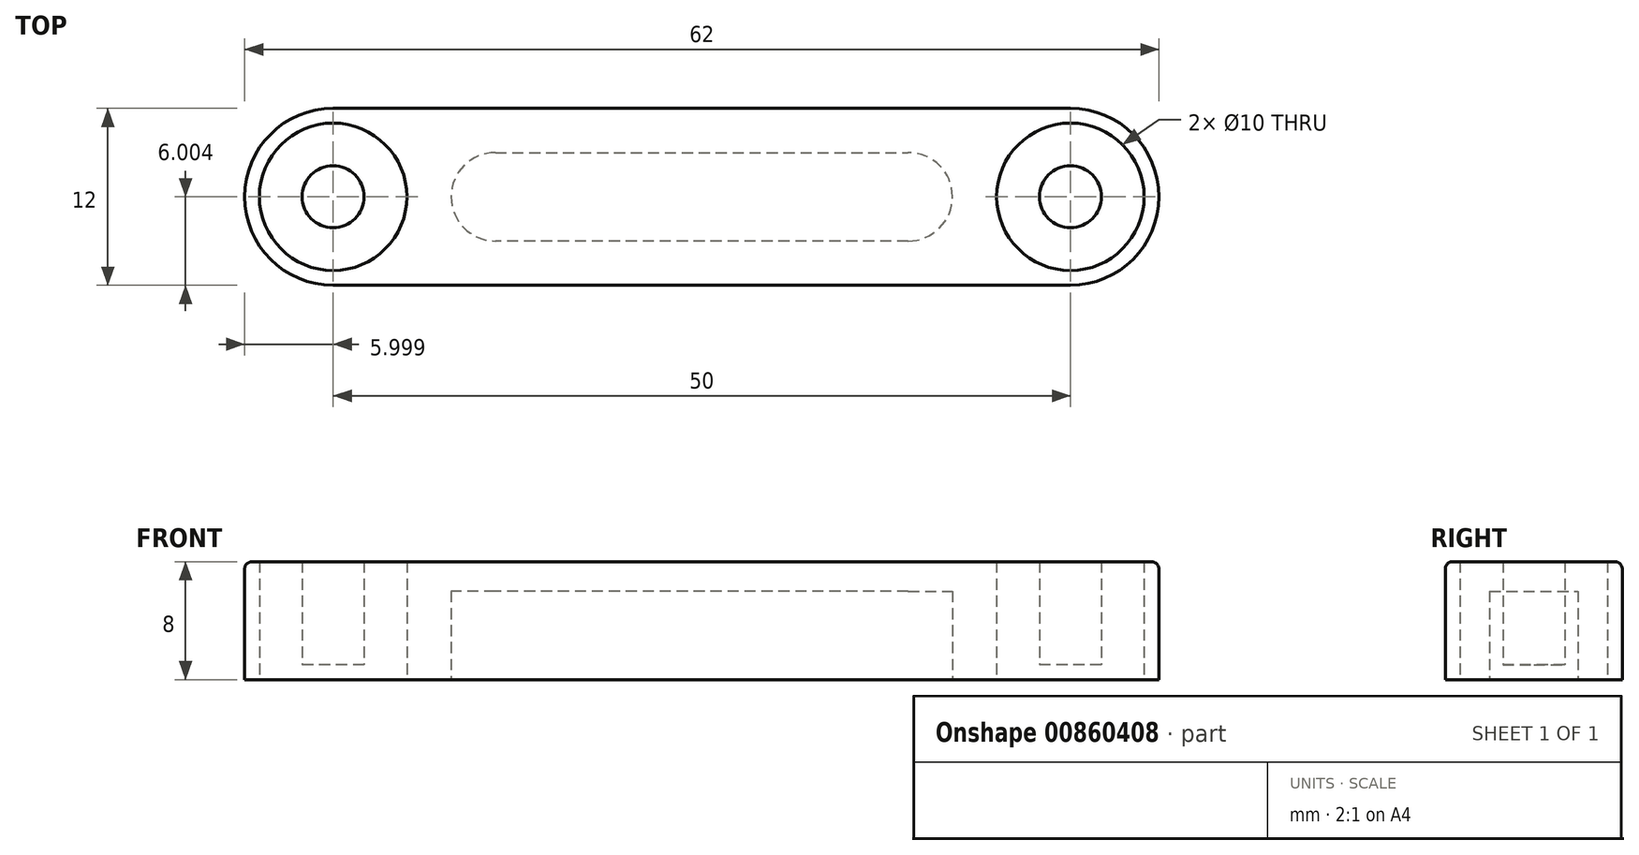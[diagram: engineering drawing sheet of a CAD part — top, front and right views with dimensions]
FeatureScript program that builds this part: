
annotation { "Feature Type Name" : "Feature", "Feature Type Description" : "" }
export const myFeature = defineFeature(function(context is Context, id is Id, definition is map)
    precondition{}
    {
        {
            var Q0;
            Q0=qCreatedBy(makeId("Top.planeOp"),FACE);
            var sketch = newSketch(context, id + "F0", { "sketchPlane" : qUnion([Q0])});
            skLineSegment(sketch, "E0", {"start": v(-96.16, -25.4) * mm, "end": v(-46.16, -25.4) * mm});
            skLineSegment(sketch, "E1", {"start": v(-46.16, -13.4) * mm, "end": v(-96.16, -13.4) * mm});
            skCircle(sketch, "E2", {"center": v(-96.16, -19.4) * mm, "radius": 2.1 * mm});
            skCircle(sketch, "E3", {"center": v(-46.16, -19.4) * mm, "radius": 2.1 * mm});
            skLineSegment(sketch, "E4", {"start": v(-9.27, -13.4) * mm, "end": v(-9.27, -25.4) * mm});
            skLineSegment(sketch, "E5", {"start": v(-1.27, -24.9) * mm, "end": v(-1.27, -13.9) * mm});
            skLineSegment(sketch, "E6", {"start": v(-1.77, -13.4) * mm, "end": v(-9.27, -13.4) * mm});
            skLineSegment(sketch, "E7", {"start": v(-9.27, -17.3) * mm, "end": v(-5.27, -17.3) * mm});
            skLineSegment(sketch, "E8", {"start": v(-9.27, -21.5) * mm, "end": v(-5.27, -21.5) * mm});
            skLineSegment(sketch, "E9", {"start": v(-5.27, -15.4) * mm, "end": v(-1.27, -15.4) * mm});
            skLineSegment(sketch, "E10", {"start": v(-5.27, -23.4) * mm, "end": v(-1.27, -23.4) * mm});
            skCircle(sketch, "E11", {"center": v(-96.16, -19.4) * mm, "radius": 4 * mm});
            skCircle(sketch, "E12", {"center": v(-46.16, -19.4) * mm, "radius": 4 * mm});
            skLineSegment(sketch, "E13", {"start": v(-5.27, -15.4) * mm, "end": v(-5.27, -23.4) * mm});
            skLineSegment(sketch, "E14", {"start": v(-85.16, -16.4) * mm, "end": v(-57.16, -16.4) * mm});
            skLineSegment(sketch, "E15", {"start": v(-57.16, -22.4) * mm, "end": v(-85.16, -22.4) * mm});
            skArc(sketch, "E16", {"start": v(-57.16, -22.4) * mm, "mid": v(-54.16, -19.4) * mm, "end": v(-57.16, -16.4) * mm});
            skArc(sketch, "E17", {"start": v(-85.16, -16.4) * mm, "mid": v(-88.16, -19.4) * mm, "end": v(-85.16, -22.4) * mm});
            skLineSegment(sketch, "E18", {"start": v(-9.27, -16.4) * mm, "end": v(-3.27, -16.4) * mm});
            skLineSegment(sketch, "E19", {"start": v(-3.27, -16.4) * mm, "end": v(-3.27, -22.4) * mm});
            skLineSegment(sketch, "E20", {"start": v(-9.27, -22.4) * mm, "end": v(-3.27, -22.4) * mm});
            skArc(sketch, "E21", {"start": v(-96.16, -13.4) * mm, "mid": v(-102.16, -19.4) * mm, "end": v(-96.16, -25.4) * mm});
            skArc(sketch, "E22", {"start": v(-46.16, -25.4) * mm, "mid": v(-40.16, -19.4) * mm, "end": v(-46.16, -13.4) * mm});
            skLineSegment(sketch, "E23", {"start": v(-46.16, -13.9) * mm, "end": v(-96.16, -13.9) * mm});
            skLineSegment(sketch, "E24", {"start": v(-96.16, -24.9) * mm, "end": v(-46.16, -24.9) * mm});
            skArc(sketch, "E25", {"start": v(-46.16, -24.9) * mm, "mid": v(-40.66, -19.4) * mm, "end": v(-46.16, -13.9) * mm});
            skArc(sketch, "E26", {"start": v(-96.16, -13.9) * mm, "mid": v(-101.66, -19.4) * mm, "end": v(-96.16, -24.9) * mm});
            skLineSegment(sketch, "E27", {"start": v(-9.27, -25.4) * mm, "end": v(-1.77, -25.4) * mm});
            skLineSegment(sketch, "E28", {"start": v(-1.77, -25.4) * mm, "end": v(-1.27, -24.9) * mm});
            skLineSegment(sketch, "E29", {"start": v(-1.77, -13.4) * mm, "end": v(-1.27, -13.9) * mm});
            skLineSegment(sketch, "E30", {"start": v(-1.77, -13.4) * mm, "end": v(-1.77, -25.4) * mm});
            skCircle(sketch, "E31", {"center": v(-46.16, -19.4) * mm, "radius": 5 * mm});
            skCircle(sketch, "E32", {"center": v(-96.16, -19.4) * mm, "radius": 5 * mm});
            skLineSegment(sketch, "E33", {"start": v(-8.27, -14.4) * mm, "end": v(-8.27, -24.4) * mm});
            skLineSegment(sketch, "E34", {"start": v(-8.27, -14.4) * mm, "end": v(-9.27, -14.4) * mm});
            skLineSegment(sketch, "E35", {"start": v(-8.27, -24.4) * mm, "end": v(-9.27, -24.4) * mm});
            skSolve(sketch);
        }
        {
            var Q0;
            Q0=makeQuery(id+"F0.imprint","IMPRINT",FACE,{"disambiguationData":[TD([[makeQuery(id+"F0.imprint","IMPRINT",EDGE,{"derivedFrom":sQuery(id+"F0.wireOp",EDGE,"E0")}),1.0]])]});
            var Q1;
            Q1=makeQuery(id+"F0.imprint","IMPRINT",FACE,{"disambiguationData":[TD([[makeQuery(id+"F0.imprint","IMPRINT",EDGE,{"derivedFrom":sQuery(id+"F0.wireOp",EDGE,"E14")}),1.0]])]});
            var Q2;
            Q2=makeQuery(id+"F0.imprint","IMPRINT",FACE,{"disambiguationData":[TD([[makeQuery(id+"F0.imprint","IMPRINT",EDGE,{"derivedFrom":sQuery(id+"F0.wireOp",EDGE,"E11")}),1.0]])]});
            var Q3;
            Q3=makeQuery(id+"F0.imprint","IMPRINT",FACE,{"disambiguationData":[TD([[makeQuery(id+"F0.imprint","IMPRINT",EDGE,{"derivedFrom":sQuery(id+"F0.wireOp",EDGE,"E2")}),1.0]])]});
            var Q4;
            Q4=makeQuery(id+"F0.imprint","IMPRINT",FACE,{"disambiguationData":[TD([[makeQuery(id+"F0.imprint","IMPRINT",EDGE,{"derivedFrom":sQuery(id+"F0.wireOp",EDGE,"E2")}),-1.0]])]});
            var Q5;
            Q5=makeQuery(id+"F0.imprint","IMPRINT",FACE,{"disambiguationData":[TD([[makeQuery(id+"F0.imprint","IMPRINT",EDGE,{"derivedFrom":sQuery(id+"F0.wireOp",EDGE,"E14")}),-1.0]])]});
            var Q6;
            Q6=makeQuery(id+"F0.imprint","IMPRINT",FACE,{"disambiguationData":[TD([[makeQuery(id+"F0.imprint","IMPRINT",EDGE,{"derivedFrom":sQuery(id+"F0.wireOp",EDGE,"E12")}),1.0]])]});
            var Q7;
            Q7=makeQuery(id+"F0.imprint","IMPRINT",FACE,{"disambiguationData":[TD([[makeQuery(id+"F0.imprint","IMPRINT",EDGE,{"derivedFrom":sQuery(id+"F0.wireOp",EDGE,"E3")}),1.0]])]});
            var Q8;
            Q8=makeQuery(id+"F0.imprint","IMPRINT",FACE,{"disambiguationData":[TD([[makeQuery(id+"F0.imprint","IMPRINT",EDGE,{"derivedFrom":sQuery(id+"F0.wireOp",EDGE,"E3")}),-1.0]])]});
            extrude(context, id + "F1", {"entities" : qUnion([Q0, Q1, Q2, Q3, Q4, Q5, Q6, Q7, Q8]), "depth" : 8 * mm, "offsetDistance" : 25 * mm});
        }
        {
            var Q0;
            Q0=makeQuery(id+"F0.imprint","IMPRINT",FACE,{"disambiguationData":[TD([[makeQuery(id+"F0.imprint","IMPRINT",EDGE,{"derivedFrom":sQuery(id+"F0.wireOp",EDGE,"E2")}),-1.0]])]});
            var Q1;
            Q1=makeQuery(id+"F0.imprint","IMPRINT",FACE,{"disambiguationData":[TD([[makeQuery(id+"F0.imprint","IMPRINT",EDGE,{"derivedFrom":sQuery(id+"F0.wireOp",EDGE,"E3")}),-1.0]])]});
            extrude(context, id + "F2", {"entities" : qUnion([Q0, Q1]), "operationType" : NewBodyOperationType.REMOVE, "depth" : 25 * mm, "offsetDistance" : 25 * mm});
        }
        {
            var Q0;
            Q0=makeQuery(id+"F1.opExtrude","CAP_FACE",FACE,{"disambiguationData":[OSD([sQuery(id+"F0.wireOp",EDGE,"E0"),sQuery(id+"F0.wireOp",EDGE,"E1"),sQuery(id+"F0.wireOp",EDGE,"E21"),sQuery(id+"F0.wireOp",EDGE,"E22")])],"isStart":false});
            var sketch = newSketch(context, id + "F3", { "sketchPlane" : qUnion([Q0])});
            skCircle(sketch, "E36.0", {"center": v(-96.16, -19.4) * mm, "radius": 4 * mm});
            skCircle(sketch, "E37.0", {"center": v(-46.16, -19.4) * mm, "radius": 4 * mm});
            skSolve(sketch);
        }
        {
            var Q0;
            Q0=makeQuery(id+"F3.imprint","IMPRINT",FACE,{"disambiguationData":[TD([[makeQuery(id+"F3.imprint","IMPRINT",EDGE,{"derivedFrom":sQuery(id+"F3.wireOp",EDGE,"E36.0")}),-1.0]])]});
            var Q1;
            Q1=makeQuery(id+"F3.imprint","IMPRINT",FACE,{"disambiguationData":[TD([[makeQuery(id+"F3.imprint","IMPRINT",EDGE,{"derivedFrom":sQuery(id+"F3.wireOp",EDGE,"E37.0")}),-1.0]])]});
            extrude(context, id + "F4", {"entities" : qUnion([Q0, Q1]), "operationType" : NewBodyOperationType.REMOVE, "oppositeDirection" : true, "depth" : 4 * mm, "offsetDistance" : 25 * mm});
        }
        {
            var Q0;
            Q0=makeQuery(id+"F0.imprint","IMPRINT",FACE,{"disambiguationData":[TD([[makeQuery(id+"F0.imprint","IMPRINT",EDGE,{"derivedFrom":sQuery(id+"F0.wireOp",EDGE,"E14")}),-1.0]])]});
            extrude(context, id + "F5", {"entities" : qUnion([Q0]), "operationType" : NewBodyOperationType.REMOVE, "depth" : 6 * mm, "offsetDistance" : 25 * mm});
        }
        {
            var Q0;
            Q0=makeQuery(id+"F0.imprint","IMPRINT",FACE,{"disambiguationData":[TD([[makeQuery(id+"F0.imprint","IMPRINT",EDGE,{"derivedFrom":sQuery(id+"F0.wireOp",EDGE,"E11")}),1.0]])]});
            var Q1;
            Q1=makeQuery(id+"F0.imprint","IMPRINT",FACE,{"disambiguationData":[TD([[makeQuery(id+"F0.imprint","IMPRINT",EDGE,{"derivedFrom":sQuery(id+"F0.wireOp",EDGE,"E2")}),1.0]])]});
            var Q2;
            Q2=makeQuery(id+"F0.imprint","IMPRINT",FACE,{"disambiguationData":[TD([[makeQuery(id+"F0.imprint","IMPRINT",EDGE,{"derivedFrom":sQuery(id+"F0.wireOp",EDGE,"E12")}),1.0]])]});
            var Q3;
            Q3=makeQuery(id+"F0.imprint","IMPRINT",FACE,{"disambiguationData":[TD([[makeQuery(id+"F0.imprint","IMPRINT",EDGE,{"derivedFrom":sQuery(id+"F0.wireOp",EDGE,"E3")}),1.0]])]});
            extrude(context, id + "F6", {"entities" : qUnion([Q0, Q1, Q2, Q3]), "operationType" : NewBodyOperationType.REMOVE, "depth" : 1 * mm, "offsetDistance" : 25 * mm});
        }
        {
            var Q0;
            Q0=makeQuery(id+"F1.opExtrude","CAP_EDGE",EDGE,{"disambiguationData":[OSD([sQuery(id+"F0.wireOp",EDGE,"E0")])],"isStart":false});
            fillet(context, id + "F7", {"entities" : qUnion([Q0]), "radius" : .5 * mm, "tangentPropagation" : true, "allowEdgeOverflow" : false});
        }
    });
